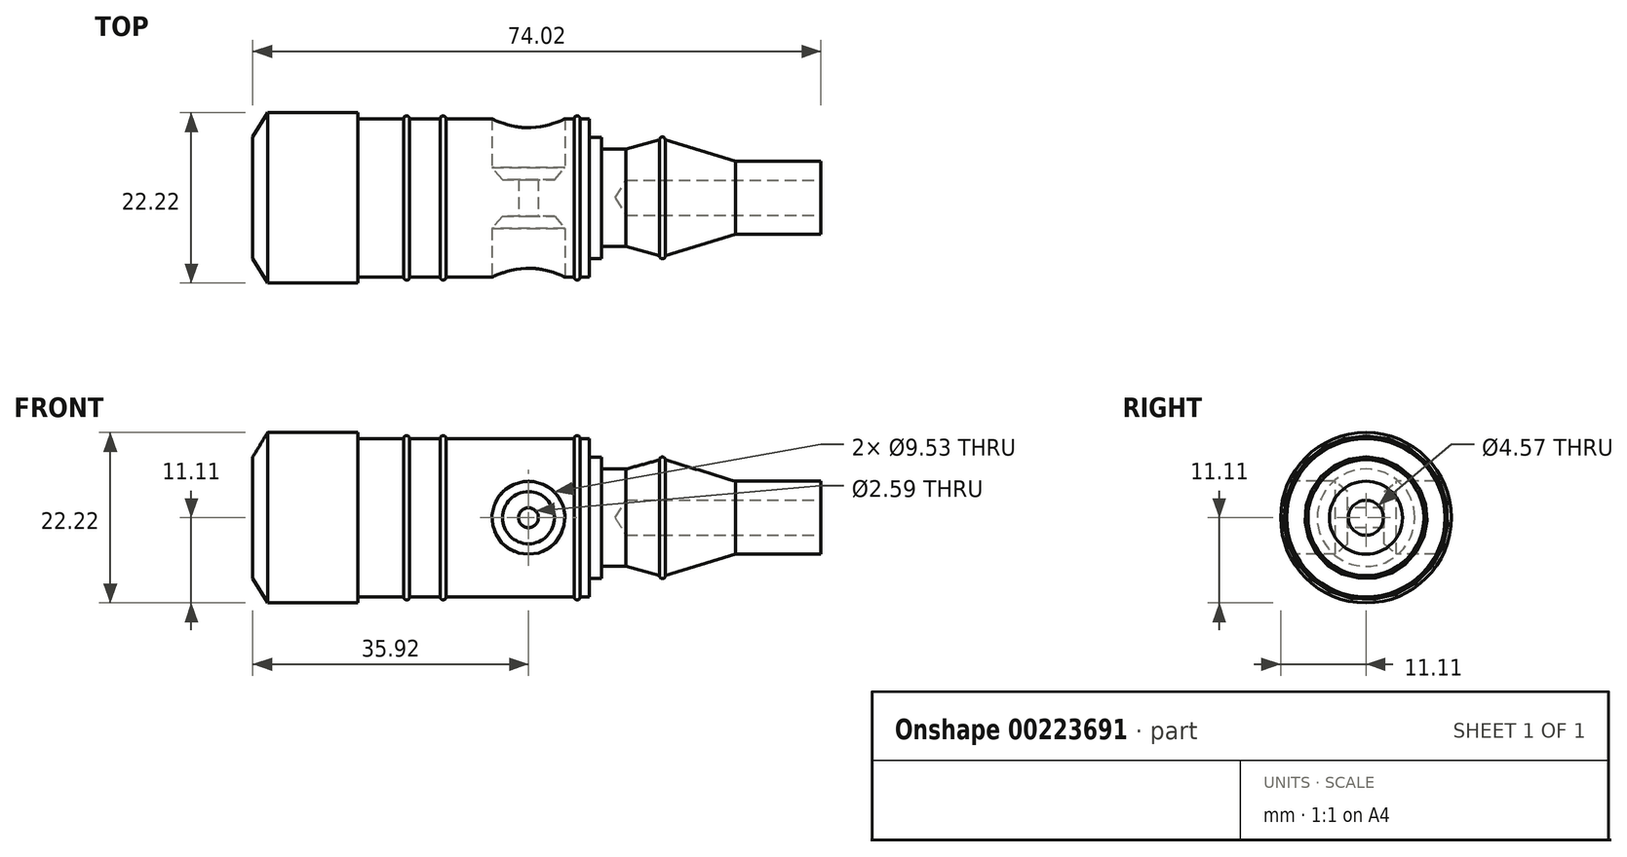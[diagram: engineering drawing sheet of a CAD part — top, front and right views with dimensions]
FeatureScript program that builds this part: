
annotation { "Feature Type Name" : "Feature", "Feature Type Description" : "" }
export const myFeature = defineFeature(function(context is Context, id is Id, definition is map)
    precondition{}
    {
        {
            var Q0;
            Q0=qCreatedBy(makeId("Front.planeOp"),FACE);
            var sketch = newSketch(context, id + "F0", { "sketchPlane" : qUnion([Q0])});
            skLineSegment(sketch, "E0", {"start": v(43.6, 4.76) * mm, "end": v(54.72, 4.76) * mm});
            skLineSegment(sketch, "E1", {"start": v(54.72, 4.76) * mm, "end": v(54.72, 0) * mm});
            skLineSegment(sketch, "E2", {"start": v(-5.6, 11.11) * mm, "end": v(-17.39, 11.11) * mm});
            skLineSegment(sketch, "E3", {"start": v(-19.3, 0) * mm, "end": v(54.72, 0) * mm});
            skLineSegment(sketch, "E4", {"start": v(33.69, 7.56) * mm, "end": v(29.44, 7.56) * mm, "construction": true});
            skLineSegment(sketch, "E5", {"start": v(29.32, 6.35) * mm, "end": v(26.14, 6.35) * mm});
            skLineSegment(sketch, "E6", {"start": v(26.14, 6.35) * mm, "end": v(26.14, 7.92) * mm});
            skLineSegment(sketch, "E7", {"start": v(26.14, 7.92) * mm, "end": v(24.54, 7.92) * mm});
            skLineSegment(sketch, "E8", {"start": v(24.54, 7.92) * mm, "end": v(24.54, 10.33) * mm});
            skLineSegment(sketch, "E9", {"start": v(24.54, 10.33) * mm, "end": v(23.35, 10.33) * mm});
            skLineSegment(sketch, "E10", {"start": v(22.59, 10.33) * mm, "end": v(5.88, 10.33) * mm});
            skLineSegment(sketch, "E11", {"start": v(5.11, 10.33) * mm, "end": v(1.13, 10.33) * mm});
            skLineSegment(sketch, "E12", {"start": v(0.36, 10.33) * mm, "end": v(-5.6, 10.33) * mm});
            skLineSegment(sketch, "E13", {"start": v(-5.6, 11.11) * mm, "end": v(-5.6, 10.33) * mm});
            skArc(sketch, "E14", {"start": v(1.13, 10.33) * mm, "mid": v(0.74, 10.7) * mm, "end": v(0.36, 10.33) * mm});
            skArc(sketch, "E15", {"start": v(5.88, 10.33) * mm, "mid": v(5.5, 10.7) * mm, "end": v(5.11, 10.33) * mm});
            skArc(sketch, "E16", {"start": v(23.35, 10.33) * mm, "mid": v(22.97, 10.7) * mm, "end": v(22.59, 10.33) * mm});
            skArc(sketch, "E17", {"start": v(34.45, 7.56) * mm, "mid": v(34.07, 7.94) * mm, "end": v(33.69, 7.56) * mm});
            skLineSegment(sketch, "E18", {"start": v(32.76, 7.94) * mm, "end": v(35.58, 7.94) * mm, "construction": true});
            skPoint(sketch, "E18.startSnap0", {"position": v(34.07, 7.94) * mm});
            skLineSegment(sketch, "E19", {"start": v(33.69, 7.56) * mm, "end": v(29.32, 6.35) * mm});
            skLineSegment(sketch, "E20", {"start": v(34.45, 7.56) * mm, "end": v(43.6, 4.76) * mm});
            skLineSegment(sketch, "E21", {"start": v(-17.39, 11.11) * mm, "end": v(-19.3, 7.94) * mm});
            skLineSegment(sketch, "E22", {"start": v(-19.3, 7.94) * mm, "end": v(-19.3, 0) * mm});
            skSolve(sketch);
        }
        {
            var Q0;
            Q0 = qSketchRegion(id + "F0", true);
            var Q1;
            Q1=sQuery(id+"F0.wireOp",EDGE,"E3");
            revolve(context, id + "F1", {"entities" : qUnion([Q0]), "axis" : qUnion([Q1]), "revolveType" : RevolveType.FULL});
        }
        {
            var Q0;
            Q0=makeQuery(id+"F1.opRevolve","SWEPT_FACE",FACE,{"disambiguationData":[OSD([sQuery(id+"F0.wireOp",EDGE,"E1")])]});
            var sketch = newSketch(context, id + "F2", { "sketchPlane" : qUnion([Q0])});
            skPoint(sketch, "E23", {"position": v(0, 0) * mm});
            skSolve(sketch);
        }
        {
            var Q0;
            Q0=sQuery(id+"F2.wireOp",VERTEX,"E23");
            var Q1;
            Q1=makeQuery(id+"F1.opRevolve","SWEPT_BODY",BODY,{"disambiguationData":[OSD([sQuery(id+"F0.wireOp",EDGE,"E0"),sQuery(id+"F0.wireOp",EDGE,"E1"),sQuery(id+"F0.wireOp",EDGE,"E2"),sQuery(id+"F0.wireOp",EDGE,"E3"),sQuery(id+"F0.wireOp",EDGE,"E5"),sQuery(id+"F0.wireOp",EDGE,"E6"),sQuery(id+"F0.wireOp",EDGE,"E7"),sQuery(id+"F0.wireOp",EDGE,"E8"),sQuery(id+"F0.wireOp",EDGE,"E9"),sQuery(id+"F0.wireOp",EDGE,"E10"),sQuery(id+"F0.wireOp",EDGE,"E11"),sQuery(id+"F0.wireOp",EDGE,"E12"),sQuery(id+"F0.wireOp",EDGE,"E13"),sQuery(id+"F0.wireOp",EDGE,"E14"),sQuery(id+"F0.wireOp",EDGE,"E15"),sQuery(id+"F0.wireOp",EDGE,"E16"),sQuery(id+"F0.wireOp",EDGE,"E17"),sQuery(id+"F0.wireOp",EDGE,"E19"),sQuery(id+"F0.wireOp",EDGE,"E20"),sQuery(id+"F0.wireOp",EDGE,"E21"),sQuery(id+"F0.wireOp",EDGE,"E22")])]});
            hole(context, id + "F3", {"style" : HoleStyle.SIMPLE, "endStyle" : HoleEndStyle.BLIND, "holeDiameter" : 4.57 * mm, "holeDepth" : 25.4 * mm, "locations" : qUnion([Q0]), "scope" : qUnion([Q1])});
        }
        {
            var Q0;
            Q0=qCreatedBy(makeId("Top.planeOp"),FACE);
            var sketch = newSketch(context, id + "F4", { "sketchPlane" : qUnion([Q0])});
            skLineSegment(sketch, "E24", {"start": v(43.6, 4.76) * mm, "end": v(54.72, 4.76) * mm});
            skLineSegment(sketch, "E25", {"start": v(54.72, -4.76) * mm, "end": v(43.6, -4.76) * mm});
            skLineSegment(sketch, "E26", {"start": v(5.88, 10.33) * mm, "end": v(22.59, 10.33) * mm});
            skLineSegment(sketch, "E27", {"start": v(22.59, -10.33) * mm, "end": v(5.88, -10.33) * mm});
            skLineSegment(sketch, "E28", {"start": v(16.62, 10.33) * mm, "end": v(16.62, -10.33) * mm});
            skPoint(sketch, "E29", {"position": v(16.62, 0) * mm});
            skLineSegment(sketch, "E30", {"start": v(11.86, 10.33) * mm, "end": v(11.86, 3.98) * mm});
            skLineSegment(sketch, "E31", {"start": v(11.86, 3.98) * mm, "end": v(13.23, 2.39) * mm});
            skLineSegment(sketch, "E32", {"start": v(13.23, 2.39) * mm, "end": v(15.32, 2.39) * mm});
            skLineSegment(sketch, "E33", {"start": v(15.32, 2.39) * mm, "end": v(15.32, -2.39) * mm});
            skLineSegment(sketch, "E34", {"start": v(15.32, -2.39) * mm, "end": v(13.23, -2.39) * mm});
            skLineSegment(sketch, "E35", {"start": v(13.23, -2.39) * mm, "end": v(11.86, -3.98) * mm});
            skLineSegment(sketch, "E36", {"start": v(11.86, -3.98) * mm, "end": v(11.86, -10.33) * mm});
            skLineSegment(sketch, "E37", {"start": v(11.86, -10.33) * mm, "end": v(16.62, -10.33) * mm});
            skLineSegment(sketch, "E38", {"start": v(16.62, 10.33) * mm, "end": v(11.86, 10.33) * mm});
            skSolve(sketch);
        }
        {
            var Q0;
            Q0 = qSketchRegion(id + "F4", true);
            var Q1;
            Q1=sQuery(id+"F4.wireOp",EDGE,"E28");
            revolve(context, id + "F5", {"operationType" : NewBodyOperationType.REMOVE, "entities" : qUnion([Q0]), "axis" : qUnion([Q1]), "revolveType" : RevolveType.FULL, "oppositeDirection" : true});
        }
    });
